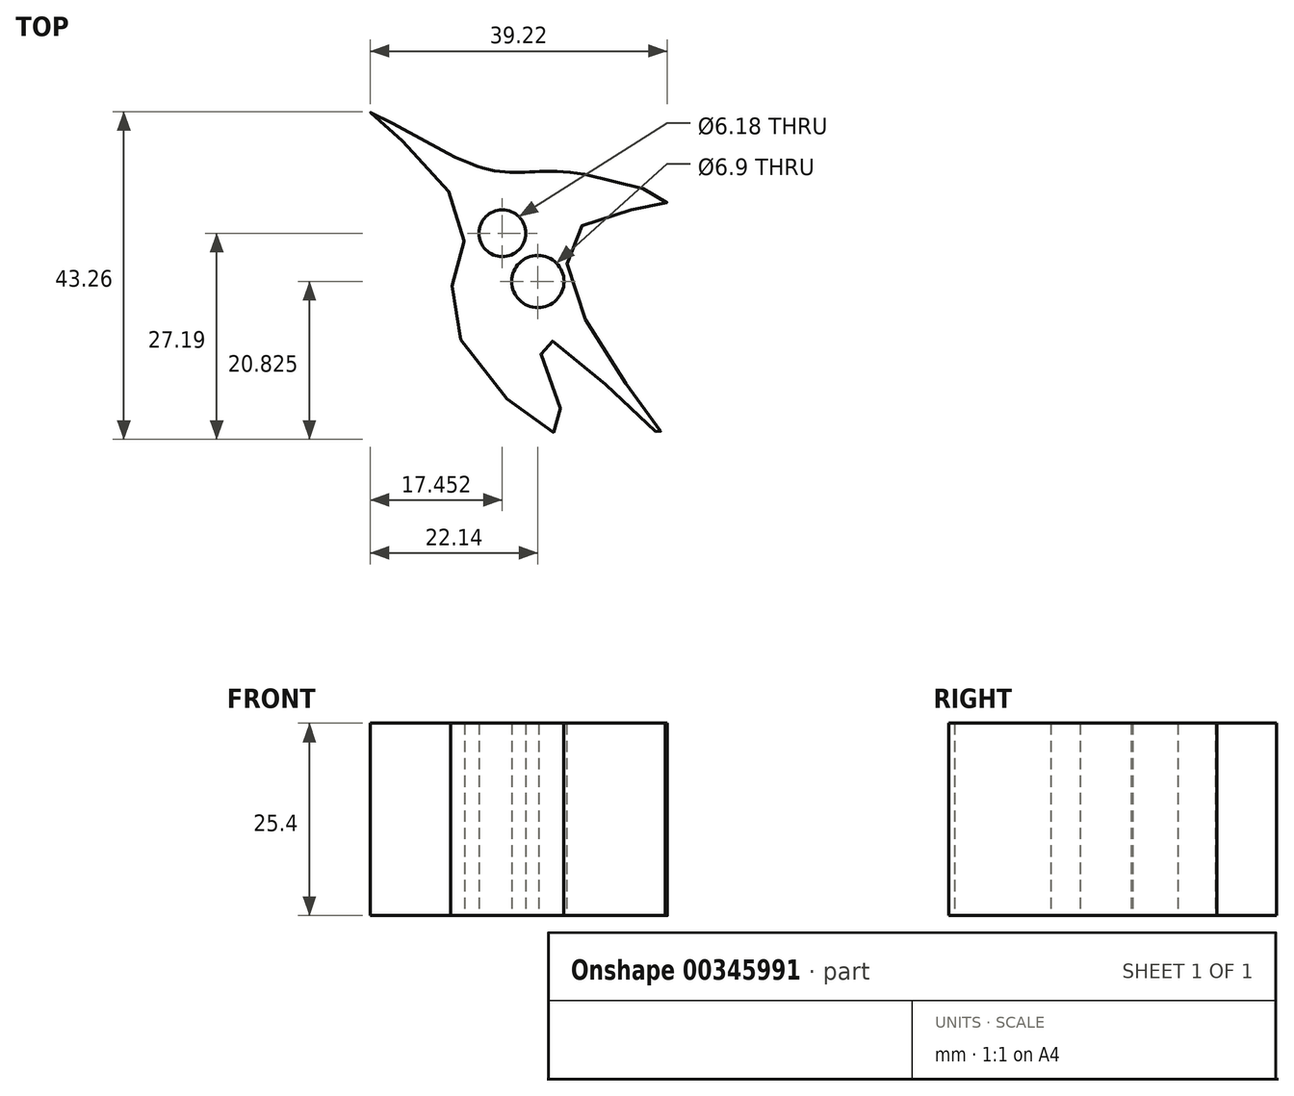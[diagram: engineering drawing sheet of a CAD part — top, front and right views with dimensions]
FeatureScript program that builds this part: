
annotation { "Feature Type Name" : "Feature", "Feature Type Description" : "" }
export const myFeature = defineFeature(function(context is Context, id is Id, definition is map)
    precondition{}
    {
        {
            var Q0;
            Q0=qCreatedBy(makeId("Top.planeOp"),FACE);
            var sketch = newSketch(context, id + "F0", { "sketchPlane" : qUnion([Q0])});
            skFitSpline(sketch, "E0", {"points": [v(-31.7, 10.67) * mm, v(-45.79, 17.84) * mm, v(-33.74, 4.26) * mm, v(-34.77, -10.09) * mm, v(-20.37, -24.23) * mm, v(-23.3, -11.99) * mm, v(-7.1, -25.27) * mm, v(-16.06, -11.99) * mm, v(-17.6, 2.98) * mm, v(-6.58, 5.94) * mm, v(-19.9, 9.9) * mm, v(-31.7, 10.67) * mm]});
            skArc(sketch, "E1", {"start": v(-17.48, 9.59) * mm, "mid": v(-23.34, 31.93) * mm, "end": v(-35.5, 12.3) * mm});
            skLineSegment(sketch, "E2", {"start": v(-32.48, 26.1) * mm, "end": v(-31.24, 24.34) * mm});
            skLineSegment(sketch, "E3", {"start": v(-31.24, 24.34) * mm, "end": v(-33.29, 22.9) * mm});
            skLineSegment(sketch, "E4", {"start": v(-33.29, 22.9) * mm, "end": v(-32.5, 21.8) * mm});
            skLineSegment(sketch, "E5", {"start": v(-32.5, 21.8) * mm, "end": v(-30.53, 23.2) * mm});
            skLineSegment(sketch, "E6", {"start": v(-30.53, 23.2) * mm, "end": v(-29.33, 21.5) * mm});
            skLineSegment(sketch, "E7", {"start": v(-29.33, 21.5) * mm, "end": v(-28.18, 22.32) * mm});
            skLineSegment(sketch, "E8", {"start": v(-28.18, 22.32) * mm, "end": v(-29.1, 23.63) * mm});
            skLineSegment(sketch, "E9", {"start": v(-29.1, 23.63) * mm, "end": v(-27.54, 24.74) * mm});
            skLineSegment(sketch, "E10", {"start": v(-27.54, 24.74) * mm, "end": v(-28.3, 25.59) * mm});
            skLineSegment(sketch, "E11", {"start": v(-28.3, 25.59) * mm, "end": v(-29.55, 25) * mm});
            skLineSegment(sketch, "E12", {"start": v(-29.55, 25) * mm, "end": v(-31.24, 26.9) * mm});
            skLineSegment(sketch, "E13", {"start": v(-31.24, 26.9) * mm, "end": v(-32.48, 26.1) * mm});
            skLineSegment(sketch, "E14", {"start": v(-20.76, 26.1) * mm, "end": v(-21.85, 27.64) * mm});
            skLineSegment(sketch, "E15", {"start": v(-21.85, 27.64) * mm, "end": v(-23.34, 26.58) * mm});
            skLineSegment(sketch, "E16", {"start": v(-23.34, 26.58) * mm, "end": v(-24.63, 28.4) * mm});
            skLineSegment(sketch, "E17", {"start": v(-24.63, 28.4) * mm, "end": v(-26.1, 26.9) * mm});
            skLineSegment(sketch, "E18", {"start": v(-26.1, 26.9) * mm, "end": v(-24.71, 24.86) * mm});
            skLineSegment(sketch, "E19", {"start": v(-24.71, 24.86) * mm, "end": v(-25.96, 23.98) * mm});
            skLineSegment(sketch, "E20", {"start": v(-25.96, 23.98) * mm, "end": v(-25.08, 22.8) * mm});
            skLineSegment(sketch, "E21", {"start": v(-25.08, 22.8) * mm, "end": v(-23.64, 23.89) * mm});
            skLineSegment(sketch, "E22", {"start": v(-23.64, 23.89) * mm, "end": v(-22.6, 22.51) * mm});
            skLineSegment(sketch, "E23", {"start": v(-22.6, 22.51) * mm, "end": v(-21.34, 23.24) * mm});
            skLineSegment(sketch, "E24", {"start": v(-21.34, 23.24) * mm, "end": v(-22.15, 24.5) * mm});
            skLineSegment(sketch, "E25", {"start": v(-22.15, 24.5) * mm, "end": v(-20.76, 26.1) * mm});
            skCircle(sketch, "E26", {"center": v(-24.2, 15.48) * mm, "radius": 3.13 * mm});
            skCircle(sketch, "E27", {"center": v(-28.34, 1.79) * mm, "radius": 3.09 * mm});
            skCircle(sketch, "E28", {"center": v(-23.65, -4.58) * mm, "radius": 3.45 * mm});
            skSolve(sketch);
        }
        {
            var Q0;
            Q0=makeQuery(id+"F0.imprint","IMPRINT",FACE,{"disambiguationData":[TD([[makeQuery(id+"F0.imprint","IMPRINT",EDGE,{"derivedFrom":sQuery(id+"F0.wireOp",EDGE,"E0")}),1.0]])]});
            extrude(context, id + "F1", {"entities" : qUnion([Q0]), "depth" : 25.4 * mm});
        }
    });
